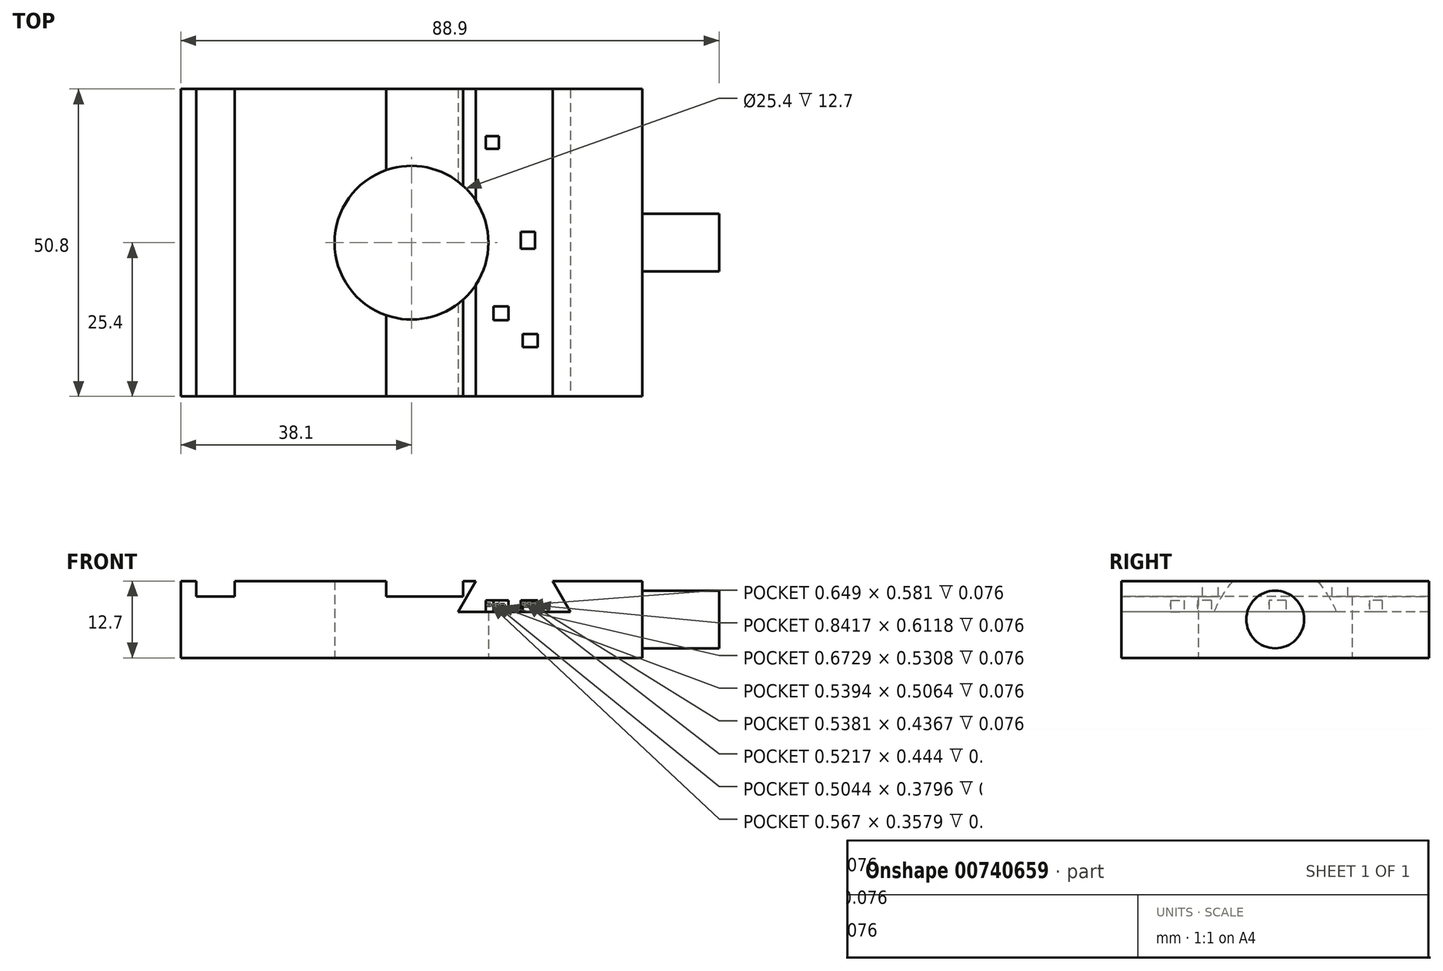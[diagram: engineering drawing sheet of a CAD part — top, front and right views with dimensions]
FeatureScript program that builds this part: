
annotation { "Feature Type Name" : "Feature", "Feature Type Description" : "" }
export const myFeature = defineFeature(function(context is Context, id is Id, definition is map)
    precondition{}
    {
        {
            var Q0;
            Q0=qCreatedBy(makeId("Top.planeOp"),FACE);
            var sketch = newSketch(context, id + "F0", { "sketchPlane" : qUnion([Q0])});
            skLineSegment(sketch, "E0.bottom", {"start": v(38.1, 25.4) * mm, "end": v(-38.1, 25.4) * mm});
            skLineSegment(sketch, "E0.top", {"start": v(38.1, -25.4) * mm, "end": v(-38.1, -25.4) * mm});
            skLineSegment(sketch, "E0.left", {"start": v(38.1, 25.4) * mm, "end": v(38.1, -25.4) * mm});
            skLineSegment(sketch, "E0.right", {"start": v(-38.1, 25.4) * mm, "end": v(-38.1, -25.4) * mm});
            skPoint(sketch, "E0.middle", {"position": v(0, 0) * mm});
            skCircle(sketch, "E1", {"center": v(0, 0) * mm, "radius": 12.7 * mm});
            skSolve(sketch);
        }
        {
            var Q0;
            Q0=makeQuery(id+"F0.imprint","IMPRINT",FACE,{"disambiguationData":[TD([[makeQuery(id+"F0.imprint","IMPRINT",EDGE,{"derivedFrom":sQuery(id+"F0.wireOp",EDGE,"E0.bottom")}),1.0]])]});
            extrude(context, id + "F1", {"entities" : qUnion([Q0]), "depth" : 12.7 * mm, "offsetDistance" : 25.4 * mm});
        }
        {
            var Q0;
            Q0=makeQuery(id+"F1.opExtrude","CAP_FACE",FACE,{"disambiguationData":[OSD([sQuery(id+"F0.wireOp",EDGE,"E0.bottom"),sQuery(id+"F0.wireOp",EDGE,"E0.top"),sQuery(id+"F0.wireOp",EDGE,"E0.left"),sQuery(id+"F0.wireOp",EDGE,"E0.right"),sQuery(id+"F0.wireOp",EDGE,"E1")])],"isStart":false});
            var sketch = newSketch(context, id + "F2", { "sketchPlane" : qUnion([Q0])});
            skLineSegment(sketch, "E2.bottom", {"start": v(-35.56, 25.4) * mm, "end": v(-29.2, 25.4) * mm});
            skLineSegment(sketch, "E2.top", {"start": v(-35.56, -25.4) * mm, "end": v(-29.2, -25.4) * mm});
            skLineSegment(sketch, "E2.left", {"start": v(-35.56, 25.4) * mm, "end": v(-35.56, -25.4) * mm});
            skLineSegment(sketch, "E2.right", {"start": v(-29.2, 25.4) * mm, "end": v(-29.2, -25.4) * mm});
            skLineSegment(sketch, "E3", {"start": v(-4.15, 25.4) * mm, "end": v(-4.15, -25.4) * mm});
            skLineSegment(sketch, "E4", {"start": v(-4.15, -25.4) * mm, "end": v(8.55, -25.4) * mm});
            skLineSegment(sketch, "E5", {"start": v(8.55, -25.4) * mm, "end": v(8.55, 25.4) * mm});
            skLineSegment(sketch, "E6", {"start": v(8.55, 25.4) * mm, "end": v(-4.15, 25.4) * mm});
            skLineSegment(sketch, "E7", {"start": v(0, 25.4) * mm, "end": v(0, -25.4) * mm, "construction": true});
            skSolve(sketch);
        }
        {
            var Q0;
            Q0=makeQuery(id+"F2.imprint","IMPRINT",FACE,{"disambiguationData":[TD([[makeQuery(id+"F2.imprint","IMPRINT",EDGE,{"derivedFrom":sQuery(id+"F2.wireOp",EDGE,"E2.bottom")}),1.0]])]});
            var Q1;
            {var subQ0=sQuery(id+"F2.wireOp",EDGE,"E4");Q1=makeQuery(id+"F2.imprint","IMPRINT",FACE,{"disambiguationData":[TD([[makeQuery(id+"F2.imprint","IMPRINT",EDGE,{"derivedFrom":subQ0}),-1.0]])]});}
            var Q2;
            {var subQ0=sQuery(id+"F2.wireOp",EDGE,"E6");Q2=makeQuery(id+"F2.imprint","IMPRINT",FACE,{"disambiguationData":[TD([[makeQuery(id+"F2.imprint","IMPRINT",EDGE,{"derivedFrom":subQ0}),1.0]])]});}
            extrude(context, id + "F3", {"entities" : qUnion([Q0, Q1, Q2]), "operationType" : NewBodyOperationType.REMOVE, "oppositeDirection" : true, "depth" : 2.54 * mm, "offsetDistance" : 25.4 * mm});
        }
        {
            var Q0;
            Q0=makeQuery(id+"F1.opExtrude","SWEPT_FACE",FACE,{"disambiguationData":[OSD([sQuery(id+"F0.wireOp",EDGE,"E0.top")])]});
            var sketch = newSketch(context, id + "F4", { "sketchPlane" : qUnion([Q0])});
            skLineSegment(sketch, "E8", {"start": v(10.63, 12.7) * mm, "end": v(7.7, 7.62) * mm});
            skLineSegment(sketch, "E9", {"start": v(7.7, 7.62) * mm, "end": v(26.26, 7.62) * mm});
            skLineSegment(sketch, "E10", {"start": v(26.26, 7.62) * mm, "end": v(23.33, 12.7) * mm});
            skLineSegment(sketch, "E11", {"start": v(23.33, 12.7) * mm, "end": v(10.63, 12.7) * mm});
            skLineSegment(sketch, "E12", {"start": v(16.98, 7.62) * mm, "end": v(16.98, 12.7) * mm, "construction": true});
            skSolve(sketch);
        }
        {
            var Q0;
            Q0=makeQuery(id+"F4.imprint","IMPRINT",FACE,{"disambiguationData":[TD([[makeQuery(id+"F4.imprint","IMPRINT",EDGE,{"derivedFrom":sQuery(id+"F4.wireOp",EDGE,"E8")}),1.0]])]});
            extrude(context, id + "F5", {"entities" : qUnion([Q0]), "operationType" : NewBodyOperationType.REMOVE, "endBound" : BoundingType.THROUGH_ALL, "oppositeDirection" : true, "depth" : 25.4 * mm, "offsetDistance" : 25.4 * mm});
        }
        {
            var Q0;
            Q0=makeQuery(id+"F1.opExtrude","SWEPT_FACE",FACE,{"disambiguationData":[OSD([sQuery(id+"F0.wireOp",EDGE,"E0.left")])]});
            var sketch = newSketch(context, id + "F6", { "sketchPlane" : qUnion([Q0])});
            skCircle(sketch, "E13", {"center": v(0, 6.35) * mm, "radius": 4.76 * mm});
            skPoint(sketch, "E13.centerSnap0", {"position": v(0, 12.7) * mm});
            skPoint(sketch, "E13.centerSnap1", {"position": v(-25.4, 6.35) * mm});
            skSolve(sketch);
        }
        {
            var Q0;
            Q0=makeQuery(id+"F6.imprint","IMPRINT",FACE,{"disambiguationData":[TD([[makeQuery(id+"F6.imprint","IMPRINT",EDGE,{"derivedFrom":sQuery(id+"F6.wireOp",EDGE,"E13")}),1.0]])]});
            extrude(context, id + "F7", {"entities" : qUnion([Q0]), "operationType" : NewBodyOperationType.ADD, "depth" : 12.7 * mm, "offsetDistance" : 25.4 * mm});
        }
        {
            var Q0;
            Q0=makeQuery(id+"F5.boolean.opBoolean","COPY",FACE,{"derivedFrom":makeQuery(id+"F5.opExtrude","SWEPT_FACE",FACE,{"disambiguationData":[OSD([sQuery(id+"F4.wireOp",EDGE,"E9")])]})});
            var sketch = newSketch(context, id + "F8", { "sketchPlane" : qUnion([Q0])});
            skLineSegment(sketch, "E14.bottom", {"start": v(12.25, 17.62) * mm, "end": v(14.44, 17.62) * mm});
            skLineSegment(sketch, "E14.top", {"start": v(12.25, 15.52) * mm, "end": v(14.44, 15.52) * mm});
            skLineSegment(sketch, "E14.left", {"start": v(12.25, 17.62) * mm, "end": v(12.25, 15.52) * mm});
            skLineSegment(sketch, "E14.right", {"start": v(14.44, 17.62) * mm, "end": v(14.44, 15.52) * mm});
            skLineSegment(sketch, "E15.bottom", {"start": v(18.02, 1.8) * mm, "end": v(20.38, 1.8) * mm});
            skLineSegment(sketch, "E15.top", {"start": v(18.02, -1) * mm, "end": v(20.38, -1) * mm});
            skLineSegment(sketch, "E15.left", {"start": v(18.02, 1.8) * mm, "end": v(18.02, -1) * mm});
            skLineSegment(sketch, "E15.right", {"start": v(20.38, 1.8) * mm, "end": v(20.38, -1) * mm});
            skLineSegment(sketch, "E16.bottom", {"start": v(13.56, -10.54) * mm, "end": v(16.01, -10.54) * mm});
            skLineSegment(sketch, "E16.top", {"start": v(13.56, -12.81) * mm, "end": v(16.01, -12.81) * mm});
            skLineSegment(sketch, "E16.left", {"start": v(13.56, -10.54) * mm, "end": v(13.56, -12.81) * mm});
            skLineSegment(sketch, "E16.right", {"start": v(16.01, -10.54) * mm, "end": v(16.01, -12.81) * mm});
            skLineSegment(sketch, "E17.bottom", {"start": v(18.37, -17.27) * mm, "end": v(20.82, -17.27) * mm});
            skLineSegment(sketch, "E17.top", {"start": v(18.37, -15.08) * mm, "end": v(20.82, -15.08) * mm});
            skLineSegment(sketch, "E17.left", {"start": v(18.37, -17.27) * mm, "end": v(18.37, -15.08) * mm});
            skLineSegment(sketch, "E17.right", {"start": v(20.82, -17.27) * mm, "end": v(20.82, -15.08) * mm});
            skSolve(sketch);
        }
        {
            var Q0;
            Q0=makeQuery(id+"F8.imprint","IMPRINT",FACE,{"disambiguationData":[TD([[makeQuery(id+"F8.imprint","IMPRINT",EDGE,{"derivedFrom":sQuery(id+"F8.wireOp",EDGE,"E14.bottom")}),-1.0]])]});
            var Q1;
            Q1=makeQuery(id+"F8.imprint","IMPRINT",FACE,{"disambiguationData":[TD([[makeQuery(id+"F8.imprint","IMPRINT",EDGE,{"derivedFrom":sQuery(id+"F8.wireOp",EDGE,"E15.bottom")}),-1.0]])]});
            var Q2;
            Q2=makeQuery(id+"F8.imprint","IMPRINT",FACE,{"disambiguationData":[TD([[makeQuery(id+"F8.imprint","IMPRINT",EDGE,{"derivedFrom":sQuery(id+"F8.wireOp",EDGE,"E16.bottom")}),-1.0]])]});
            var Q3;
            Q3=makeQuery(id+"F8.imprint","IMPRINT",FACE,{"disambiguationData":[TD([[makeQuery(id+"F8.imprint","IMPRINT",EDGE,{"derivedFrom":sQuery(id+"F8.wireOp",EDGE,"E17.bottom")}),1.0]])]});
            extrude(context, id + "F9", {"entities" : qUnion([Q0, Q1, Q2, Q3]), "operationType" : NewBodyOperationType.ADD, "depth" : 1.9 * mm, "offsetDistance" : 25.4 * mm});
        }
        {
            var Q0;
            Q0=makeQuery(id+"F9.opExtrude","SWEPT_FACE",FACE,{"disambiguationData":[OSD([sQuery(id+"F8.wireOp",EDGE,"E17.bottom")])]});
            var sketch = newSketch(context, id + "F10", { "sketchPlane" : qUnion([Q0])});
            skLineSegment(sketch, "E18.bottom", {"start": v(18.61, 8.5) * mm, "end": v(19.26, 8.5) * mm});
            skLineSegment(sketch, "E18.top", {"start": v(18.61, 9.08) * mm, "end": v(19.26, 9.08) * mm});
            skLineSegment(sketch, "E18.left", {"start": v(18.61, 8.5) * mm, "end": v(18.61, 9.08) * mm});
            skLineSegment(sketch, "E18.right", {"start": v(19.26, 8.5) * mm, "end": v(19.26, 9.08) * mm});
            skLineSegment(sketch, "E19.bottom", {"start": v(19.65, 8.46) * mm, "end": v(20.49, 8.46) * mm});
            skLineSegment(sketch, "E19.top", {"start": v(19.65, 9.08) * mm, "end": v(20.49, 9.08) * mm});
            skLineSegment(sketch, "E19.left", {"start": v(19.65, 8.46) * mm, "end": v(19.65, 9.08) * mm});
            skLineSegment(sketch, "E19.right", {"start": v(20.49, 8.46) * mm, "end": v(20.49, 9.08) * mm});
            skSolve(sketch);
        }
        {
            var Q0;
            Q0=makeQuery(id+"F10.imprint","IMPRINT",FACE,{"disambiguationData":[TD([[makeQuery(id+"F10.imprint","IMPRINT",EDGE,{"derivedFrom":sQuery(id+"F10.wireOp",EDGE,"E19.bottom")}),1.0]])]});
            var Q1;
            Q1=makeQuery(id+"F10.imprint","IMPRINT",FACE,{"disambiguationData":[TD([[makeQuery(id+"F10.imprint","IMPRINT",EDGE,{"derivedFrom":sQuery(id+"F10.wireOp",EDGE,"E18.bottom")}),1.0]])]});
            extrude(context, id + "F11", {"entities" : qUnion([Q0, Q1]), "operationType" : NewBodyOperationType.REMOVE, "oppositeDirection" : true, "depth" : 0.08 * mm, "offsetDistance" : 25.4 * mm});
        }
        {
            var Q0;
            Q0=makeQuery(id+"F9.opExtrude","SWEPT_FACE",FACE,{"disambiguationData":[OSD([sQuery(id+"F8.wireOp",EDGE,"E16.top")])]});
            var sketch = newSketch(context, id + "F12", { "sketchPlane" : qUnion([Q0])});
            skLineSegment(sketch, "E20.bottom", {"start": v(13.83, 8.39) * mm, "end": v(14.36, 8.39) * mm});
            skLineSegment(sketch, "E20.top", {"start": v(13.83, 8.9) * mm, "end": v(14.36, 8.9) * mm});
            skLineSegment(sketch, "E20.left", {"start": v(13.83, 8.39) * mm, "end": v(13.83, 8.9) * mm});
            skLineSegment(sketch, "E20.right", {"start": v(14.36, 8.39) * mm, "end": v(14.36, 8.9) * mm});
            skLineSegment(sketch, "E21.bottom", {"start": v(14.7, 8.37) * mm, "end": v(15.37, 8.37) * mm});
            skLineSegment(sketch, "E21.top", {"start": v(14.7, 8.9) * mm, "end": v(15.37, 8.9) * mm});
            skLineSegment(sketch, "E21.left", {"start": v(14.7, 8.37) * mm, "end": v(14.7, 8.9) * mm});
            skLineSegment(sketch, "E21.right", {"start": v(15.37, 8.37) * mm, "end": v(15.37, 8.9) * mm});
            skSolve(sketch);
        }
        {
            var Q0;
            Q0 = qSketchRegion(id + "F12", true);
            extrude(context, id + "F13", {"entities" : qUnion([Q0]), "operationType" : NewBodyOperationType.REMOVE, "oppositeDirection" : true, "depth" : 0.08 * mm, "offsetDistance" : 25.4 * mm});
        }
        {
            var Q0;
            Q0=makeQuery(id+"F9.opExtrude","SWEPT_FACE",FACE,{"disambiguationData":[OSD([sQuery(id+"F8.wireOp",EDGE,"E15.top")])]});
            var sketch = newSketch(context, id + "F14", { "sketchPlane" : qUnion([Q0])});
            skLineSegment(sketch, "E22.bottom", {"start": v(18.33, 8.71) * mm, "end": v(18.85, 8.71) * mm});
            skLineSegment(sketch, "E22.top", {"start": v(18.33, 9.16) * mm, "end": v(18.85, 9.16) * mm});
            skLineSegment(sketch, "E22.left", {"start": v(18.33, 8.71) * mm, "end": v(18.33, 9.16) * mm});
            skLineSegment(sketch, "E22.right", {"start": v(18.85, 8.71) * mm, "end": v(18.85, 9.16) * mm});
            skLineSegment(sketch, "E23.bottom", {"start": v(19.15, 8.72) * mm, "end": v(19.69, 8.72) * mm});
            skLineSegment(sketch, "E23.top", {"start": v(19.15, 9.16) * mm, "end": v(19.69, 9.16) * mm});
            skLineSegment(sketch, "E23.left", {"start": v(19.15, 8.72) * mm, "end": v(19.15, 9.16) * mm});
            skLineSegment(sketch, "E23.right", {"start": v(19.69, 8.72) * mm, "end": v(19.69, 9.16) * mm});
            skSolve(sketch);
        }
        {
            var Q0;
            Q0 = qSketchRegion(id + "F14", true);
            extrude(context, id + "F15", {"entities" : qUnion([Q0]), "operationType" : NewBodyOperationType.REMOVE, "oppositeDirection" : true, "depth" : 0.08 * mm, "offsetDistance" : 25.4 * mm});
        }
        {
            var Q0;
            Q0=makeQuery(id+"F9.opExtrude","SWEPT_FACE",FACE,{"disambiguationData":[OSD([sQuery(id+"F8.wireOp",EDGE,"E14.top")])]});
            var sketch = newSketch(context, id + "F16", { "sketchPlane" : qUnion([Q0])});
            skLineSegment(sketch, "E24.bottom", {"start": v(12.51, 8.6) * mm, "end": v(13.08, 8.6) * mm});
            skLineSegment(sketch, "E24.top", {"start": v(12.51, 8.95) * mm, "end": v(13.08, 8.95) * mm});
            skLineSegment(sketch, "E24.left", {"start": v(12.51, 8.6) * mm, "end": v(12.51, 8.95) * mm});
            skLineSegment(sketch, "E24.right", {"start": v(13.08, 8.6) * mm, "end": v(13.08, 8.95) * mm});
            skLineSegment(sketch, "E25.bottom", {"start": v(13.42, 8.57) * mm, "end": v(13.92, 8.57) * mm});
            skLineSegment(sketch, "E25.top", {"start": v(13.42, 8.95) * mm, "end": v(13.92, 8.95) * mm});
            skLineSegment(sketch, "E25.left", {"start": v(13.42, 8.57) * mm, "end": v(13.42, 8.95) * mm});
            skLineSegment(sketch, "E25.right", {"start": v(13.92, 8.57) * mm, "end": v(13.92, 8.95) * mm});
            skSolve(sketch);
        }
        {
            var Q0;
            Q0 = qSketchRegion(id + "F16", true);
            extrude(context, id + "F17", {"entities" : qUnion([Q0]), "operationType" : NewBodyOperationType.REMOVE, "oppositeDirection" : true, "depth" : 0.08 * mm, "offsetDistance" : 25.4 * mm});
        }
    });
